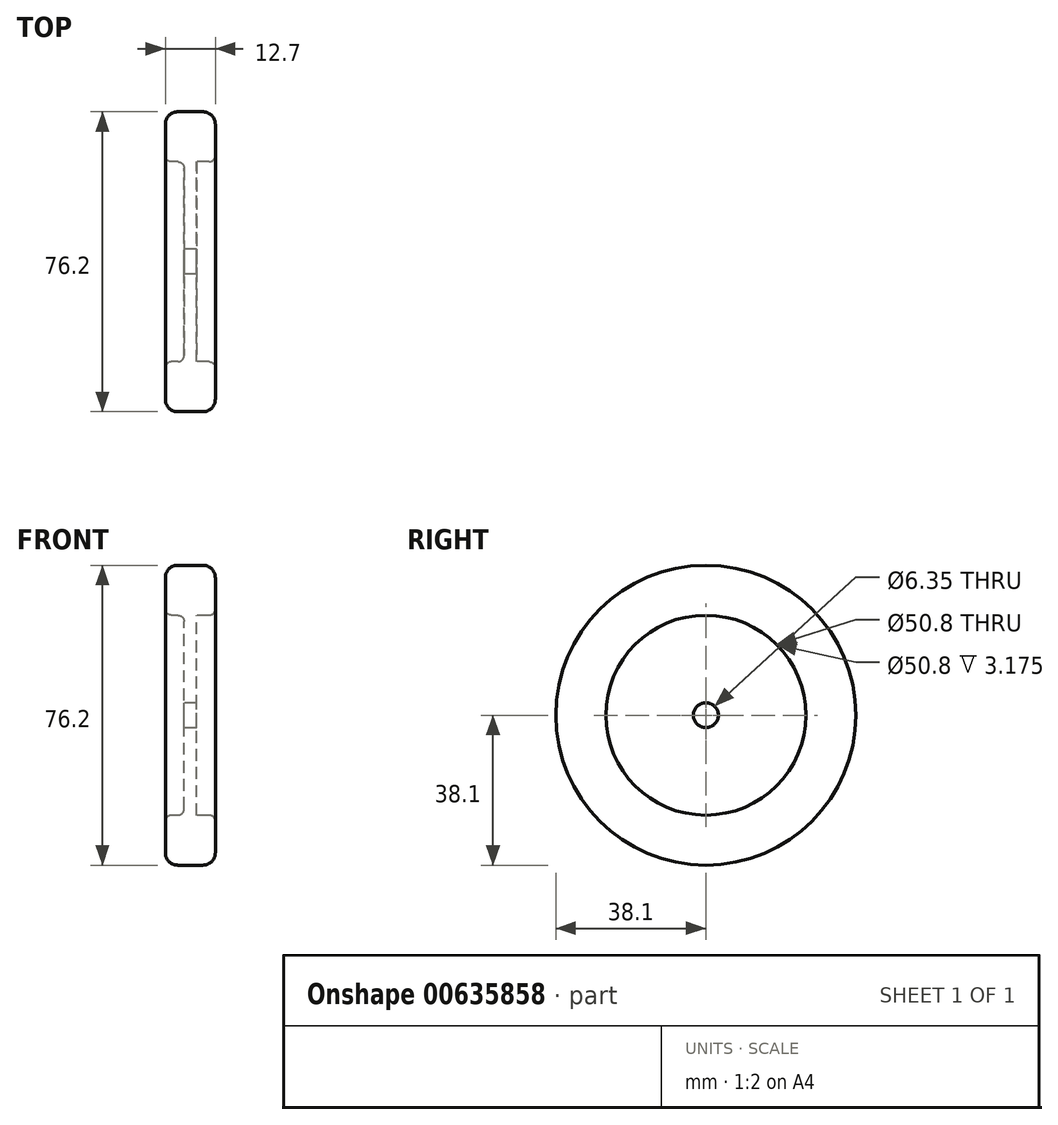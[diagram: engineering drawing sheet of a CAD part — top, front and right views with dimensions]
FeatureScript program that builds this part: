
annotation { "Feature Type Name" : "Feature", "Feature Type Description" : "" }
export const myFeature = defineFeature(function(context is Context, id is Id, definition is map)
    precondition{}
    {
        {
            var Q0;
            Q0=qCreatedBy(makeId("Right.planeOp"),FACE);
            var sketch = newSketch(context, id + "F0", { "sketchPlane" : qUnion([Q0])});
            skCircle(sketch, "E0", {"center": v(0, 0) * mm, "radius": 38.1 * mm});
            skCircle(sketch, "E1", {"center": v(0, 0) * mm, "radius": 25.4 * mm});
            skCircle(sketch, "E2", {"center": v(0, 0) * mm, "radius": 3.18 * mm});
            skSolve(sketch);
        }
        {
            var Q0;
            Q0=makeQuery(id+"F0.imprint","IMPRINT",FACE,{"disambiguationData":[TD([[makeQuery(id+"F0.imprint","IMPRINT",EDGE,{"derivedFrom":sQuery(id+"F0.wireOp",EDGE,"E1")}),1.0]])]});
            extrude(context, id + "F1", {"entities" : qUnion([Q0]), "endBound" : BoundingType.SYMMETRIC, "depth" : 3.17 * mm, "offsetDistance" : 25.4 * mm});
        }
        {
            var Q0;
            Q0 = qSketchRegion(id + "F0", true);
            extrude(context, id + "F2", {"entities" : qUnion([Q0]), "operationType" : NewBodyOperationType.ADD, "endBound" : BoundingType.SYMMETRIC, "depth" : 12.7 * mm, "offsetDistance" : 25.4 * mm});
        }
        {
            var Q0;
            Q0=makeQuery(id+"F2.opExtrude","CAP_EDGE",EDGE,{"disambiguationData":[OSD([sQuery(id+"F0.wireOp",EDGE,"E0")])],"isStart":true});
            var Q1;
            Q1=makeQuery(id+"F2.opExtrude","CAP_EDGE",EDGE,{"disambiguationData":[OSD([sQuery(id+"F0.wireOp",EDGE,"E0")])],"isStart":false});
            fillet(context, id + "F3", {"entities" : qUnion([Q0, Q1]), "radius" : 3.17 * mm, "tangentPropagation" : true, "allowEdgeOverflow" : false});
        }
        {
            var Q0;
            Q0=makeQuery(id+"F1.opExtrude","CAP_EDGE",EDGE,{"disambiguationData":[OSD([sQuery(id+"F0.wireOp",EDGE,"E1")])],"isStart":false});
            var Q1;
            Q1=makeQuery(id+"F2.opExtrude","CAP_EDGE",EDGE,{"disambiguationData":[OSD([sQuery(id+"F0.wireOp",EDGE,"E1")])],"isStart":false});
            var Q2;
            Q2=makeQuery(id+"F1.opExtrude","CAP_EDGE",EDGE,{"disambiguationData":[OSD([sQuery(id+"F0.wireOp",EDGE,"E1")])],"isStart":true});
            var Q3;
            Q3=makeQuery(id+"F2.opExtrude","CAP_EDGE",EDGE,{"disambiguationData":[OSD([sQuery(id+"F0.wireOp",EDGE,"E1")])],"isStart":true});
            fillet(context, id + "F4", {"entities" : qUnion([Q0, Q1, Q2, Q3]), "radius" : 1.59 * mm, "tangentPropagation" : true, "allowEdgeOverflow" : false});
        }
    });
